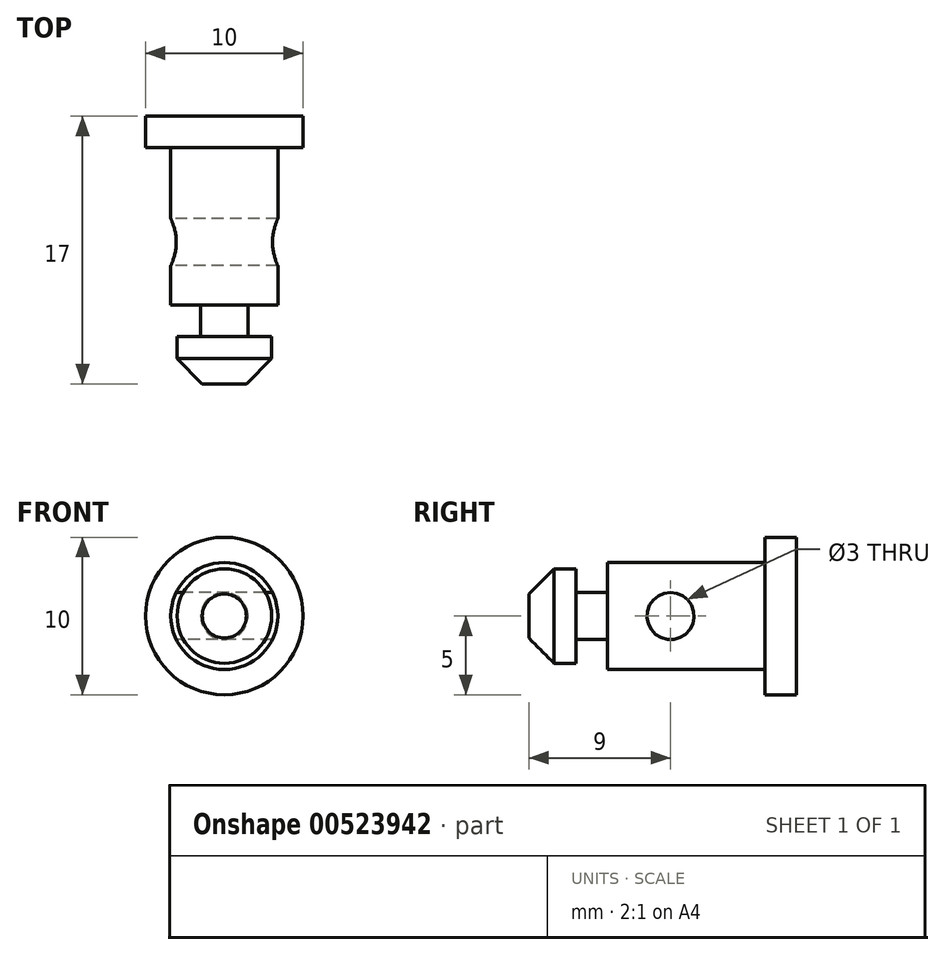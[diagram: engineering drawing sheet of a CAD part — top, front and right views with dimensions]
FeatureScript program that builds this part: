
annotation { "Feature Type Name" : "Feature", "Feature Type Description" : "" }
export const myFeature = defineFeature(function(context is Context, id is Id, definition is map)
    precondition{}
    {
        {
            var Q0;
            Q0=qCreatedBy(makeId("Front.planeOp"),FACE);
            var sketch = newSketch(context, id + "F0", { "sketchPlane" : qUnion([Q0])});
            skCircle(sketch, "E0", {"center": v(0, 0) * mm, "radius": 5 * mm});
            skSolve(sketch);
        }
        {
            var Q0;
            Q0 = qSketchRegion(id + "F0", true);
            extrude(context, id + "F1", {"entities" : qUnion([Q0]), "depth" : 2 * mm, "offsetDistance" : 25 * mm});
        }
        {
            var Q0;
            Q0=makeQuery(id+"F1.opExtrude","CAP_FACE",FACE,{"disambiguationData":[OSD([sQuery(id+"F0.wireOp",EDGE,"E0")])],"isStart":false});
            var sketch = newSketch(context, id + "F2", { "sketchPlane" : qUnion([Q0])});
            skCircle(sketch, "E1", {"center": v(0, 0) * mm, "radius": 3.4 * mm});
            skSolve(sketch);
        }
        {
            var Q0;
            Q0 = qSketchRegion(id + "F2", true);
            extrude(context, id + "F3", {"entities" : qUnion([Q0]), "operationType" : NewBodyOperationType.ADD, "depth" : 15 * mm, "offsetDistance" : 25 * mm});
        }
        {
            var Q0;
            Q0=qCreatedBy(makeId("Front.planeOp"),FACE);
            cPlane(context, id + "F4", {"entities" : qUnion([Q0]), "cplaneType" : CPlaneType.OFFSET, "offset" : 12 * mm, "width" : 150 * mm, "height" : 150 * mm});
        }
        {
            var Q0;
            Q0=qCreatedBy(id+"F4.planeOp",FACE);
            var sketch = newSketch(context, id + "F5", { "sketchPlane" : qUnion([Q0])});
            skCircle(sketch, "E2", {"center": v(0, 0) * mm, "radius": 1.5 * mm});
            skCircle(sketch, "E3", {"center": v(0, 0) * mm, "radius": 3.75 * mm});
            skSolve(sketch);
        }
        {
            var Q0;
            Q0 = qSketchRegion(id + "F5", true);
            extrude(context, id + "F6", {"entities" : qUnion([Q0]), "operationType" : NewBodyOperationType.REMOVE, "depth" : 2 * mm, "offsetDistance" : 25 * mm});
        }
        {
            var Q0;
            Q0=qCreatedBy(makeId("Right.planeOp"),FACE);
            var sketch = newSketch(context, id + "F7", { "sketchPlane" : qUnion([Q0])});
            skCircle(sketch, "E4", {"center": v(-8, 0) * mm, "radius": 1.5 * mm});
            skSolve(sketch);
        }
        {
            var Q0;
            Q0 = qSketchRegion(id + "F7", true);
            extrude(context, id + "F8", {"entities" : qUnion([Q0]), "operationType" : NewBodyOperationType.REMOVE, "depth" : 25 * mm, "offsetDistance" : 25 * mm, "hasSecondDirection" : true, "secondDirectionOppositeDirection" : true, "secondDirectionDepth" : 25 * mm});
        }
        {
            var Q0;
            Q0=makeQuery(id+"F3.opExtrude","CAP_EDGE",EDGE,{"disambiguationData":[OSD([sQuery(id+"F2.wireOp",EDGE,"E1")])],"isStart":false});
            chamfer(context, id + "F9", {"entities" : qUnion([Q0]), "width" : 2 * mm, "tangentPropagation" : true});
        }
        {
            var Q0;
            Q0=makeQuery(id+"F3.opExtrude","CAP_FACE",FACE,{"disambiguationData":[OSD([sQuery(id+"F2.wireOp",EDGE,"E1")])],"isStart":false});
            var sketch = newSketch(context, id + "F10", { "sketchPlane" : qUnion([Q0])});
            skCircle(sketch, "E5", {"center": v(0, 0) * mm, "radius": 3.5 * mm});
            skCircle(sketch, "E6", {"center": v(0, 0) * mm, "radius": 3 * mm});
            skSolve(sketch);
        }
        {
            var Q0;
            Q0=makeQuery(id+"F10.imprint","IMPRINT",FACE,{"disambiguationData":[TD([[makeQuery(id+"F10.imprint","IMPRINT",EDGE,{"derivedFrom":sQuery(id+"F10.wireOp",EDGE,"E5")}),1.0]])]});
            extrude(context, id + "F11", {"entities" : qUnion([Q0]), "operationType" : NewBodyOperationType.REMOVE, "oppositeDirection" : true, "depth" : 5 * mm, "offsetDistance" : 25 * mm});
        }
    });
